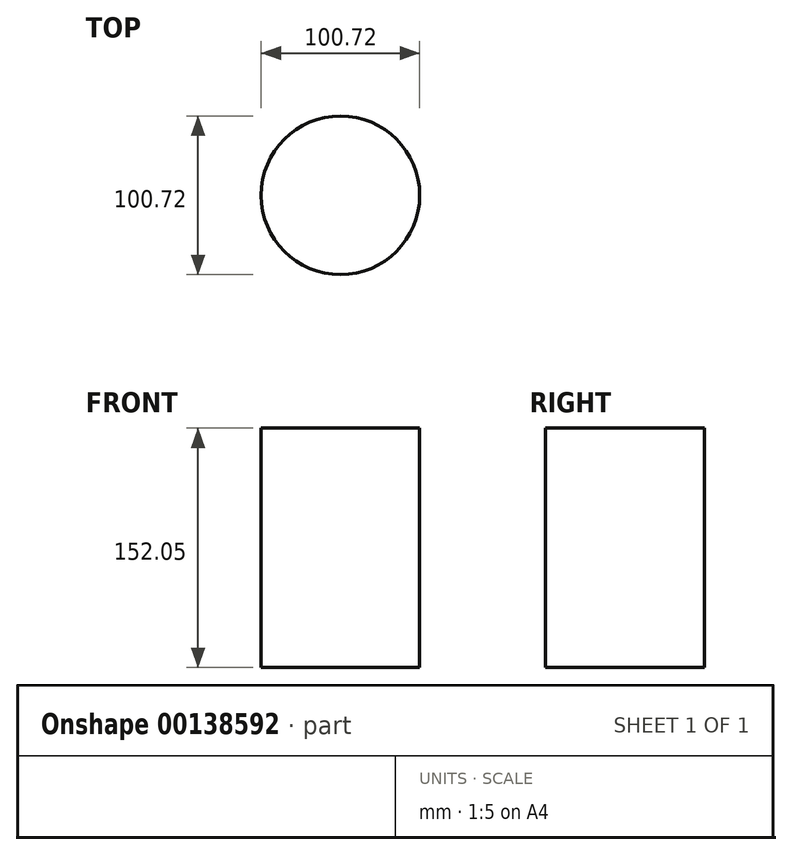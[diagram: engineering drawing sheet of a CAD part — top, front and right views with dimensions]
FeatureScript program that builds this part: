
annotation { "Feature Type Name" : "Feature", "Feature Type Description" : "" }
export const myFeature = defineFeature(function(context is Context, id is Id, definition is map)
    precondition{}
    {
        {
            var Q0;
            Q0=qCreatedBy(makeId("Top.planeOp"),FACE);
            var sketch = newSketch(context, id + "F0", { "sketchPlane" : qUnion([Q0])});
            skCircle(sketch, "E0", {"center": v(0, 0) * mm, "radius": 50.36 * mm});
            skSolve(sketch);
        }
        {
            var Q0;
            Q0=makeQuery(id+"F0.imprint","IMPRINT",FACE,{"disambiguationData":[TD([[makeQuery(id+"F0.imprint","IMPRINT",EDGE,{"derivedFrom":sQuery(id+"F0.wireOp",EDGE,"E0")}),1.0]])]});
            extrude(context, id + "F1", {"entities" : qUnion([Q0]), "depth" : 76.03 * mm, "hasSecondDirection" : true, "secondDirectionOppositeDirection" : true, "secondDirectionDepth" : 76.02 * mm});
        }
    });
